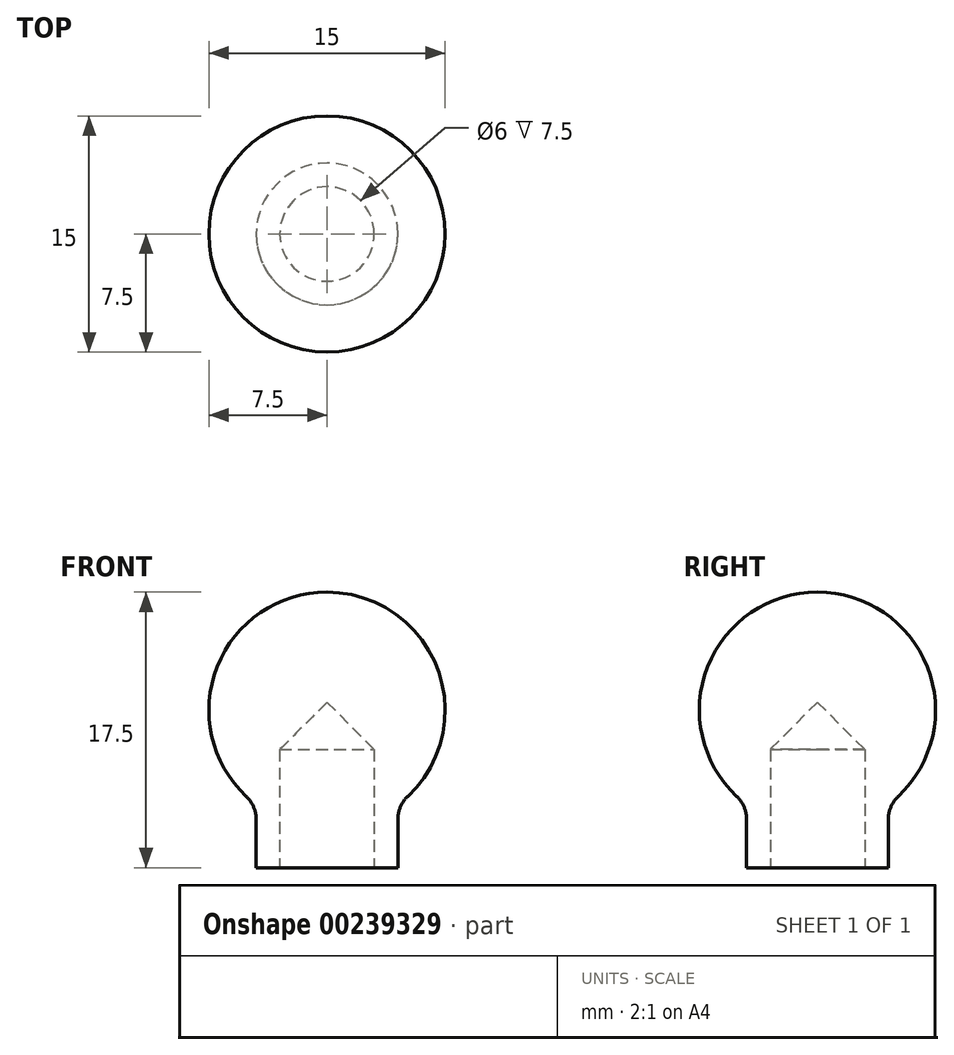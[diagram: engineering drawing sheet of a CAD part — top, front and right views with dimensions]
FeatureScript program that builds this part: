
annotation { "Feature Type Name" : "Feature", "Feature Type Description" : "" }
export const myFeature = defineFeature(function(context is Context, id is Id, definition is map)
    precondition{}
    {
        {
            var Q0;
            Q0=qCreatedBy(makeId("Front.planeOp"),FACE);
            var sketch = newSketch(context, id + "F0", { "sketchPlane" : qUnion([Q0])});
            skLineSegment(sketch, "E0", {"start": v(3, 0) * mm, "end": v(4.5, 0) * mm});
            skLineSegment(sketch, "E1", {"start": v(4.5, 0) * mm, "end": v(4.5, 4) * mm});
            skArc(sketch, "E2", {"start": v(4.5, 4) * mm, "mid": v(7.12, 12.37) * mm, "end": v(0, 17.5) * mm});
            skLineSegment(sketch, "E3", {"start": v(0, 10.5) * mm, "end": v(0, 17.5) * mm});
            skLineSegment(sketch, "E4", {"start": v(3, 0) * mm, "end": v(3, 7.5) * mm});
            skLineSegment(sketch, "E5.MirrorCS", {"start": v(-3, 0) * mm, "end": v(-3, 7.5) * mm, "construction": true});
            skLineSegment(sketch, "E6", {"start": v(3, 7.5) * mm, "end": v(0, 10.5) * mm});
            skPoint(sketch, "E7.MirrorCS.start.orphan", {"position": v(-3, 7.5) * mm});
            skSolve(sketch);
        }
        {
            var Q0;
            Q0 = qSketchRegion(id + "F0", true);
            var Q1;
            Q1=sQuery(id+"F0.wireOp",EDGE,"E3");
            revolve(context, id + "F1", {"entities" : qUnion([Q0]), "axis" : qUnion([Q1]), "revolveType" : RevolveType.FULL});
        }
        {
            var Q0;
            Q0=makeQuery(id+"F1.opRevolve","SWEPT_EDGE",EDGE,{"disambiguationData":[OSD([sQuery(id+"F0.wireOp",EDGE,"E1"),sQuery(id+"F0.wireOp",EDGE,"E2")])]});
            fillet(context, id + "F2", {"entities" : qUnion([Q0]), "radius" : 2 * mm, "tangentPropagation" : true, "allowEdgeOverflow" : false});
        }
    });
